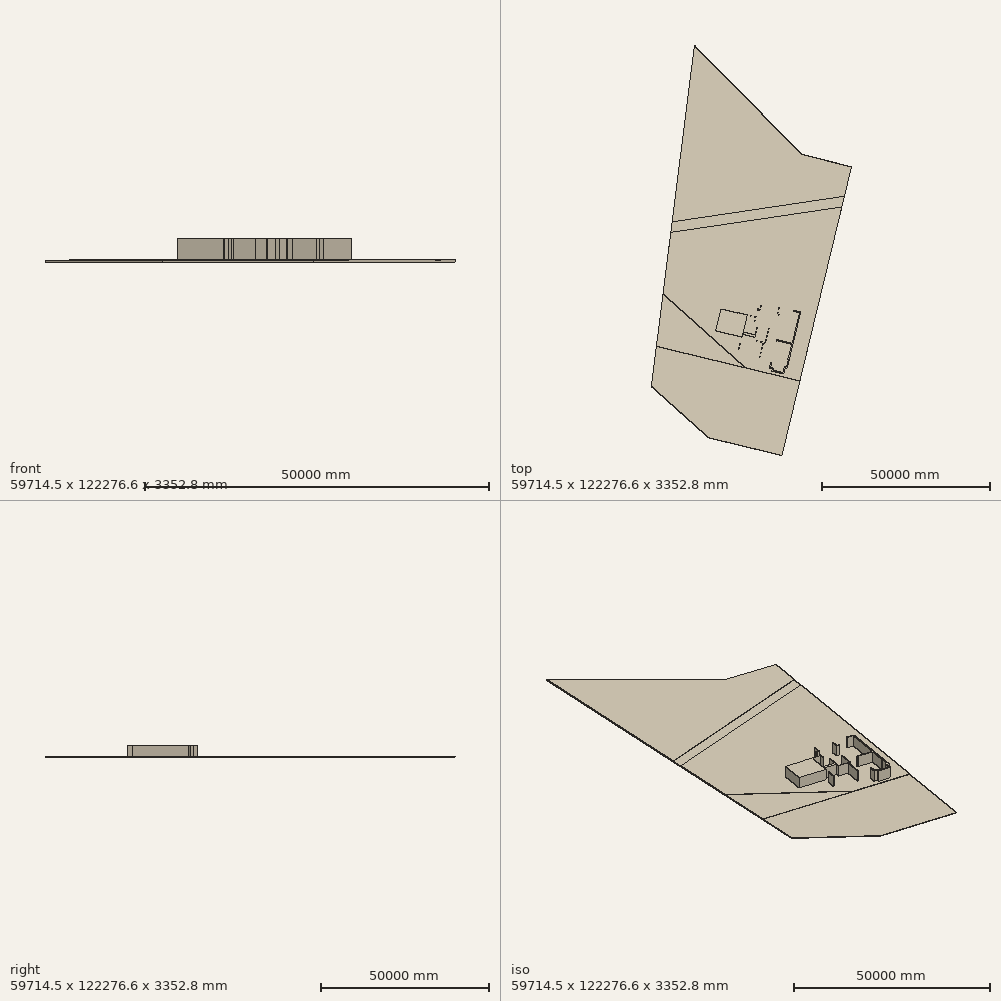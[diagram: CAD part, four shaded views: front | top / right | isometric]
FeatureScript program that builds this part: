
annotation { "Feature Type Name" : "Feature", "Feature Type Description" : "" }
export const myFeature = defineFeature(function(context is Context, id is Id, definition is map)
    precondition{}
    {
        {
            var Q0;
            Q0=qCreatedBy(makeId("Top.planeOp"),FACE);
            var sketch = newSketch(context, id + "F0", { "sketchPlane" : qUnion([Q0])});
            skLineSegment(sketch, "E0", {"start": v(0, 0) * mm, "end": v(31989.83, -32467.96) * mm});
            skLineSegment(sketch, "E1", {"start": v(31989.83, -32467.96) * mm, "end": v(46862.18, -36229.17) * mm});
            skLineSegment(sketch, "E2", {"start": v(46862.18, -36229.17) * mm, "end": v(26112.23, -122276.56) * mm});
            skLineSegment(sketch, "E3", {"start": v(46862.18, -36229.17) * mm, "end": v(46862.18, -51469.17) * mm, "construction": true});
            skLineSegment(sketch, "E4", {"start": v(0, 0) * mm, "end": v(-12852.3, -101676.89) * mm});
            skLineSegment(sketch, "E5", {"start": v(0, 0) * mm, "end": v(0, 15240) * mm, "construction": true});
            skLineSegment(sketch, "E6", {"start": v(26112.23, -122276.56) * mm, "end": v(4230, -116999.76) * mm});
            skLineSegment(sketch, "E7", {"start": v(26112.23, -122276.56) * mm, "end": v(10872.23, -122276.56) * mm, "construction": true});
            skLineSegment(sketch, "E8", {"start": v(4230, -116999.76) * mm, "end": v(-12852.3, -101676.89) * mm});
            skArc(sketch, "E9", {"start": v(-4165.07, -109469.35) * mm, "mid": v(-689.73, -114039.67) * mm, "end": v(4230, -116999.76) * mm, "construction": true});
            skArc(sketch, "E10", {"start": v(-4165.07, -109469.35) * mm, "mid": v(-8132.26, -105153.47) * mm, "end": v(-12852.3, -101676.89) * mm, "construction": true});
            skLineSegment(sketch, "E11", {"start": v(31471.2, -100053.58) * mm, "end": v(-11342.08, -89729.35) * mm});
            skLineSegment(sketch, "E12", {"start": v(-9365.85, -74095.03) * mm, "end": v(15198.72, -96129.54) * mm});
            skLineSegment(sketch, "E13", {"start": v(-6651.63, -52622.31) * mm, "end": v(44754.67, -44968.73) * mm});
            skLineSegment(sketch, "E14", {"start": v(-7048.63, -55763.02) * mm, "end": v(43983.88, -48165.09) * mm});
            skSolve(sketch);
        }
        {
            var Q0;
            {var subQ4=sQuery(id+"F0.wireOp",EDGE,"E0");Q0=makeQuery(id+"F0.imprint","IMPRINT",FACE,{"disambiguationData":[TD([[makeQuery(id+"F0.imprint","IMPRINT",EDGE,{"derivedFrom":subQ4}),-1.0]])]});}
            var Q1;
            {var subQ0=sQuery(id+"F0.wireOp",EDGE,"E13");Q1=makeQuery(id+"F0.imprint","IMPRINT",FACE,{"disambiguationData":[TD([[makeQuery(id+"F0.imprint","IMPRINT",EDGE,{"derivedFrom":subQ0}),-1.0]])]});}
            var Q2;
            {var subQ0=sQuery(id+"F0.wireOp",EDGE,"E12");Q2=makeQuery(id+"F0.imprint","IMPRINT",FACE,{"disambiguationData":[TD([[makeQuery(id+"F0.imprint","IMPRINT",EDGE,{"derivedFrom":subQ0}),1.0]])]});}
            var Q3;
            {var subQ3=sQuery(id+"F0.wireOp",EDGE,"E12");Q3=makeQuery(id+"F0.imprint","IMPRINT",FACE,{"disambiguationData":[TD([[makeQuery(id+"F0.imprint","IMPRINT",EDGE,{"derivedFrom":subQ3}),-1.0]])]});}
            var Q4;
            {var subQ1=sQuery(id+"F0.wireOp",EDGE,"E6");Q4=makeQuery(id+"F0.imprint","IMPRINT",FACE,{"disambiguationData":[TD([[makeQuery(id+"F0.imprint","IMPRINT",EDGE,{"derivedFrom":subQ1}),-1.0]])]});}
            extrude(context, id + "F1", {"entities" : qUnion([Q0, Q1, Q2, Q3, Q4]), "depth" : 304.8 * mm, "offsetDistance" : 25.4 * mm});
        }
        {
            var Q0;
            Q0=makeQuery(id+"F1.opExtrude","CAP_FACE",FACE,{"disambiguationData":[OSD([sQuery(id+"F0.wireOp",EDGE,"E0"),sQuery(id+"F0.wireOp",EDGE,"E1"),sQuery(id+"F0.wireOp",EDGE,"E2"),sQuery(id+"F0.wireOp",EDGE,"E4"),sQuery(id+"F0.wireOp",EDGE,"E6"),sQuery(id+"F0.wireOp",EDGE,"E8")])],"isStart":false});
            var sketch = newSketch(context, id + "F2", { "sketchPlane" : qUnion([Q0])});
            skLineSegment(sketch, "E15.0", {"start": v(-9365.85, -74095.03) * mm, "end": v(15198.72, -96129.54) * mm});
            skLineSegment(sketch, "E16.0", {"start": v(31471.2, -100053.58) * mm, "end": v(-11342.08, -89729.35) * mm});
            skLineSegment(sketch, "E17.0", {"start": v(0, 0) * mm, "end": v(-12852.3, -101676.89) * mm});
            skSolve(sketch);
        }
        {
            var Q0;
            {var subQ0=sQuery(id+"F2.wireOp",EDGE,"E15.0");Q0=makeQuery(id+"F2.imprint","IMPRINT",FACE,{"disambiguationData":[TD([[makeQuery(id+"F2.imprint","IMPRINT",EDGE,{"derivedFrom":subQ0}),-1.0]])]});}
            extrude(context, id + "F3", {"entities" : qUnion([Q0]), "operationType" : NewBodyOperationType.REMOVE, "oppositeDirection" : true, "depth" : 76.2 * mm, "offsetDistance" : 25.4 * mm});
        }
        {
            var Q0;
            Q0=makeQuery(id+"F1.opExtrude","CAP_FACE",FACE,{"disambiguationData":[OSD([sQuery(id+"F0.wireOp",EDGE,"E0"),sQuery(id+"F0.wireOp",EDGE,"E1"),sQuery(id+"F0.wireOp",EDGE,"E2"),sQuery(id+"F0.wireOp",EDGE,"E4"),sQuery(id+"F0.wireOp",EDGE,"E6"),sQuery(id+"F0.wireOp",EDGE,"E8")])],"isStart":false});
            var sketch = newSketch(context, id + "F4", { "sketchPlane" : qUnion([Q0])});
            skLineSegment(sketch, "E18.0", {"start": v(0, 0) * mm, "end": v(-12852.3, -101676.89) * mm});
            skLineSegment(sketch, "E19.0", {"start": v(4230, -116999.76) * mm, "end": v(-12852.3, -101676.89) * mm});
            skLineSegment(sketch, "E20.0", {"start": v(26112.23, -122276.56) * mm, "end": v(4230, -116999.76) * mm});
            skLineSegment(sketch, "E21.0", {"start": v(46862.18, -36229.17) * mm, "end": v(26112.23, -122276.56) * mm});
            skLineSegment(sketch, "E22.0", {"start": v(31471.2, -100053.58) * mm, "end": v(-11342.08, -89729.35) * mm});
            skSolve(sketch);
        }
        {
            var Q0;
            {var subQ4=sQuery(id+"F4.wireOp",EDGE,"E19.0");Q0=makeQuery(id+"F4.imprint","IMPRINT",FACE,{"disambiguationData":[TD([[makeQuery(id+"F4.imprint","IMPRINT",EDGE,{"derivedFrom":subQ4}),-1.0]])]});}
            extrude(context, id + "F5", {"entities" : qUnion([Q0]), "operationType" : NewBodyOperationType.REMOVE, "oppositeDirection" : true, "depth" : 152.4 * mm, "offsetDistance" : 25.4 * mm});
        }
        {
            var Q0;
            Q0=makeQuery(id+"F1.opExtrude","CAP_FACE",FACE,{"disambiguationData":[OSD([sQuery(id+"F0.wireOp",EDGE,"E0"),sQuery(id+"F0.wireOp",EDGE,"E1"),sQuery(id+"F0.wireOp",EDGE,"E2"),sQuery(id+"F0.wireOp",EDGE,"E4"),sQuery(id+"F0.wireOp",EDGE,"E6"),sQuery(id+"F0.wireOp",EDGE,"E8")])],"isStart":false});
            var sketch = newSketch(context, id + "F6", { "sketchPlane" : qUnion([Q0])});
            skLineSegment(sketch, "E23.0", {"start": v(-6651.63, -52622.31) * mm, "end": v(44754.67, -44968.73) * mm});
            skLineSegment(sketch, "E24.0", {"start": v(-7048.63, -55763.02) * mm, "end": v(43983.88, -48165.09) * mm});
            skLineSegment(sketch, "E25.0", {"start": v(0, 0) * mm, "end": v(-12852.3, -101676.89) * mm});
            skLineSegment(sketch, "E26.0", {"start": v(46862.18, -36229.17) * mm, "end": v(26112.23, -122276.56) * mm});
            skSolve(sketch);
        }
        {
            var Q0;
            {var subQ0=sQuery(id+"F6.wireOp",EDGE,"E23.0");Q0=makeQuery(id+"F6.imprint","IMPRINT",FACE,{"disambiguationData":[TD([[makeQuery(id+"F6.imprint","IMPRINT",EDGE,{"derivedFrom":subQ0}),-1.0]])]});}
            extrude(context, id + "F7", {"entities" : qUnion([Q0]), "operationType" : NewBodyOperationType.REMOVE, "oppositeDirection" : true, "depth" : 152.4 * mm, "offsetDistance" : 25.4 * mm});
        }
        {
            var Q0;
            {var subQ0=sQuery(id+"F0.wireOp",EDGE,"E4");var subQ1=sQuery(id+"F0.wireOp",EDGE,"E2");Q0=makeQuery(id+"F7.boolean.opBoolean","SPLIT",FACE,{"disambiguationData":[TD([makeQuery(id+"F3.boolean.opBoolean","COPY",FACE,{"derivedFrom":makeQuery(id+"F3.opExtrude","SWEPT_FACE",FACE,{"disambiguationData":[OSD([sQuery(id+"F2.wireOp",EDGE,"E15.0")])]})})])],"derivedFrom":makeQuery(id+"F1.opExtrude","CAP_FACE",FACE,{"disambiguationData":[OSD([sQuery(id+"F0.wireOp",EDGE,"E0"),sQuery(id+"F0.wireOp",EDGE,"E1"),subQ1,subQ0,sQuery(id+"F0.wireOp",EDGE,"E6"),sQuery(id+"F0.wireOp",EDGE,"E8")])],"isStart":false})});}
            var sketch = newSketch(context, id + "F8", { "sketchPlane" : qUnion([Q0])});
            skLineSegment(sketch, "E27", {"start": v(27669.68, -96315.03) * mm, "end": v(31724.64, -79499.64) * mm});
            skPoint(sketch, "E28.orphan", {"position": v(31471.2, -100053.58) * mm});
            skLineSegment(sketch, "E29", {"start": v(-5717.12, -79311.3) * mm, "end": v(3764.68, -81597.8) * mm});
            skLineSegment(sketch, "E30", {"start": v(3764.68, -81597.8) * mm, "end": v(7766.05, -65004.64) * mm});
            skLineSegment(sketch, "E31", {"start": v(7766.05, -65004.64) * mm, "end": v(-1715.76, -62718.14) * mm});
            skLineSegment(sketch, "E32", {"start": v(-1715.76, -62718.14) * mm, "end": v(-5717.12, -79311.3) * mm});
            skLineSegment(sketch, "E33", {"start": v(-5145.5, -76940.85) * mm, "end": v(-2182.44, -77655.38) * mm});
            skLineSegment(sketch, "E34", {"start": v(-2182.44, -77655.38) * mm, "end": v(-2754.06, -80025.83) * mm});
            skLineSegment(sketch, "E35", {"start": v(-5145.5, -76940.85) * mm, "end": v(-9590.1, -75869.05) * mm});
            skLineSegment(sketch, "E36", {"start": v(-2182.44, -77655.38) * mm, "end": v(1247.3, -63432.67) * mm});
            skLineSegment(sketch, "E37", {"start": v(4934.3, -91780.7) * mm, "end": v(-10343.91, -88096.42) * mm});
            skLineSegment(sketch, "E38.0", {"start": v(4230, -116999.76) * mm, "end": v(-12852.3, -101676.89) * mm});
            skLineSegment(sketch, "E39", {"start": v(-2047.33, -90097.1) * mm, "end": v(-6264.7, -107585.98) * mm});
            skLineSegment(sketch, "E40", {"start": v(-5603, -89239.67) * mm, "end": v(-9358.03, -104811.25) * mm});
            skArc(sketch, "E41", {"start": v(-6746.26, -93980.57) * mm, "mid": v(-7326.44, -90293.4) * mm, "end": v(-10343.91, -88096.42) * mm});
            skLineSegment(sketch, "E42", {"start": v(-8087.58, -78739.68) * mm, "end": v(-10343.91, -88096.42) * mm});
            skLineSegment(sketch, "E43", {"start": v(-5717.12, -79311.3) * mm, "end": v(-8087.58, -78739.68) * mm});
            skLineSegment(sketch, "E44", {"start": v(22775.38, -94507.71) * mm, "end": v(22346.66, -96285.55) * mm});
            skLineSegment(sketch, "E45", {"start": v(22346.66, -96285.55) * mm, "end": v(23235.58, -96499.91) * mm});
            skLineSegment(sketch, "E46", {"start": v(23235.58, -96499.91) * mm, "end": v(23092.67, -97092.52) * mm});
            skLineSegment(sketch, "E47", {"start": v(23092.67, -97092.52) * mm, "end": v(26648.35, -97949.96) * mm});
            skLineSegment(sketch, "E48", {"start": v(26648.35, -97949.96) * mm, "end": v(27077.07, -96172.12) * mm});
            skLineSegment(sketch, "E49", {"start": v(12775.04, -92096.18) * mm, "end": v(13945.08, -87244.16) * mm});
            skLineSegment(sketch, "E50", {"start": v(13945.08, -87244.16) * mm, "end": v(5981.84, -85323.86) * mm});
            skLineSegment(sketch, "E51", {"start": v(5981.84, -85323.86) * mm, "end": v(7696.71, -78212.5) * mm});
            skLineSegment(sketch, "E52", {"start": v(14020.33, -75230.32) * mm, "end": v(31724.64, -79499.64) * mm});
            skLineSegment(sketch, "E53.trimOffspring", {"start": v(27077.07, -96172.12) * mm, "end": v(27669.68, -96315.03) * mm});
            skLineSegment(sketch, "E54.0", {"start": v(6349.6, -85099) * mm, "end": v(7921.57, -78580.26) * mm});
            skLineSegment(sketch, "E54.1", {"start": v(23460.43, -96867.67) * mm, "end": v(26423.5, -97582.2) * mm});
            skLineSegment(sketch, "E54.2", {"start": v(26423.5, -97582.2) * mm, "end": v(26852.22, -95804.36) * mm});
            skLineSegment(sketch, "E54.3", {"start": v(26852.22, -95804.36) * mm, "end": v(27444.83, -95947.27) * mm});
            skLineSegment(sketch, "E54.4", {"start": v(27444.83, -95947.27) * mm, "end": v(28016.45, -93576.82) * mm});
            skLineSegment(sketch, "E54.5", {"start": v(23603.34, -96275.06) * mm, "end": v(23460.43, -96867.67) * mm});
            skLineSegment(sketch, "E54.6", {"start": v(14245.18, -75598.08) * mm, "end": v(19282.4, -76812.78) * mm});
            skLineSegment(sketch, "E54.7", {"start": v(22714.42, -96060.7) * mm, "end": v(23603.34, -96275.06) * mm});
            skLineSegment(sketch, "E54.8", {"start": v(23143.14, -94282.86) * mm, "end": v(22714.42, -96060.7) * mm});
            skLineSegment(sketch, "E54.9", {"start": v(13142.8, -91871.32) * mm, "end": v(23143.14, -94282.86) * mm});
            skLineSegment(sketch, "E54.10", {"start": v(13142.8, -91871.32) * mm, "end": v(14312.84, -87019.3) * mm});
            skLineSegment(sketch, "E54.11", {"start": v(14312.84, -87019.3) * mm, "end": v(6349.6, -85099) * mm});
            skLineSegment(sketch, "E55", {"start": v(20619.6, -88657.73) * mm, "end": v(19476.35, -93398.63) * mm});
            skLineSegment(sketch, "E56.0", {"start": v(20508.48, -88630.93) * mm, "end": v(19365.23, -93371.83) * mm});
            skLineSegment(sketch, "E57", {"start": v(17505, -84183.4) * mm, "end": v(18255.26, -81072.19) * mm});
            skLineSegment(sketch, "E58", {"start": v(17821.54, -83358.32) * mm, "end": v(19393.5, -76839.58) * mm});
            skLineSegment(sketch, "E59", {"start": v(7921.57, -78580.26) * mm, "end": v(18255.26, -81072.19) * mm});
            skLineSegment(sketch, "E60", {"start": v(14020.33, -75230.32) * mm, "end": v(12993.2, -79489.73) * mm});
            skLineSegment(sketch, "E61", {"start": v(12993.2, -79489.73) * mm, "end": v(7696.71, -78212.5) * mm});
            skLineSegment(sketch, "E62", {"start": v(14245.18, -75598.08) * mm, "end": v(13218.05, -79857.49) * mm});
            skLineSegment(sketch, "E63", {"start": v(13244.84, -79746.37) * mm, "end": v(18282.05, -80961.07) * mm});
            skLineSegment(sketch, "E64", {"start": v(23143.14, -94282.86) * mm, "end": v(23571.86, -92505.02) * mm});
            skLineSegment(sketch, "E65", {"start": v(23032.02, -94256.07) * mm, "end": v(24603.99, -87737.32) * mm});
            skLineSegment(sketch, "E66", {"start": v(24175.27, -89515.16) * mm, "end": v(20619.6, -88657.73) * mm});
            skLineSegment(sketch, "E67", {"start": v(19833.61, -91917.1) * mm, "end": v(21018.84, -92202.9) * mm});
            skLineSegment(sketch, "E68", {"start": v(21018.84, -92202.9) * mm, "end": v(21519, -90128.76) * mm});
            skLineSegment(sketch, "E69", {"start": v(21519, -90128.76) * mm, "end": v(23889.46, -90700.39) * mm});
            skLineSegment(sketch, "E70", {"start": v(23571.86, -92505.02) * mm, "end": v(28016.45, -93576.82) * mm});
            skLineSegment(sketch, "E71", {"start": v(23828.5, -92253.37) * mm, "end": v(27982.96, -93255.2) * mm});
            skLineSegment(sketch, "E72.trimOffspring", {"start": v(18282.05, -80961.07) * mm, "end": v(19282.4, -76812.78) * mm});
            skLineSegment(sketch, "E73", {"start": v(28983.3, -89106.91) * mm, "end": v(24828.84, -88105.08) * mm});
            skLineSegment(sketch, "E74", {"start": v(27982.96, -93255.2) * mm, "end": v(28983.3, -89106.91) * mm});
            skLineSegment(sketch, "E75", {"start": v(23828.5, -92253.37) * mm, "end": v(24828.84, -88105.08) * mm});
            skLineSegment(sketch, "E76.trimOffspring", {"start": v(29159.7, -88835.91) * mm, "end": v(31356.88, -79724.5) * mm});
            skLineSegment(sketch, "E77", {"start": v(29159.7, -88835.91) * mm, "end": v(24603.99, -87737.32) * mm});
            skLineSegment(sketch, "E78", {"start": v(26023.36, -78438.34) * mm, "end": v(24951.57, -82882.93) * mm});
            skLineSegment(sketch, "E79", {"start": v(24951.57, -82882.93) * mm, "end": v(30285.09, -84169.09) * mm});
            skLineSegment(sketch, "E80", {"start": v(25912.25, -78411.54) * mm, "end": v(24340.28, -84930.28) * mm});
            skLineSegment(sketch, "E81", {"start": v(24924.77, -82994.05) * mm, "end": v(30258.3, -84280.2) * mm});
            skLineSegment(sketch, "E82", {"start": v(21057.5, -78390.48) * mm, "end": v(23724.26, -79033.55) * mm});
            skLineSegment(sketch, "E83", {"start": v(23724.26, -79033.55) * mm, "end": v(23474.18, -80070.63) * mm});
            skLineSegment(sketch, "E84", {"start": v(23474.18, -80070.63) * mm, "end": v(20807.42, -79427.55) * mm});
            skLineSegment(sketch, "E85", {"start": v(20807.42, -79427.55) * mm, "end": v(21057.5, -78390.48) * mm});
            skLineSegment(sketch, "E86", {"start": v(12993.2, -79489.73) * mm, "end": v(12921.74, -79786.03) * mm});
            skLineSegment(sketch, "E87", {"start": v(17821.54, -83358.32) * mm, "end": v(24340.28, -84930.28) * mm});
            skLineSegment(sketch, "E88", {"start": v(25961.85, -83244.13) * mm, "end": v(25553.97, -84935.55) * mm});
            skLineSegment(sketch, "E89", {"start": v(17794.75, -83469.43) * mm, "end": v(24424.6, -85068.2) * mm});
            skLineSegment(sketch, "E90", {"start": v(24424.6, -85068.2) * mm, "end": v(24924.77, -82994.05) * mm});
            skLineSegment(sketch, "E91", {"start": v(25054.81, -81967.22) * mm, "end": v(24462.2, -81824.31) * mm});
            skLineSegment(sketch, "E92", {"start": v(24462.2, -81824.31) * mm, "end": v(23890.58, -84194.76) * mm});
            skLineSegment(sketch, "E93", {"start": v(23890.58, -84194.76) * mm, "end": v(18927.44, -82997.93) * mm});
            skLineSegment(sketch, "E94", {"start": v(18807.15, -81871.54) * mm, "end": v(19128.68, -80538.16) * mm});
            skLineSegment(sketch, "E95", {"start": v(19128.68, -80538.16) * mm, "end": v(18536.07, -80395.25) * mm});
            skLineSegment(sketch, "E96", {"start": v(20165.76, -80788.24) * mm, "end": v(19879.94, -81973.47) * mm});
            skLineSegment(sketch, "E97", {"start": v(19879.94, -81973.47) * mm, "end": v(23139.32, -82759.45) * mm});
            skLineSegment(sketch, "E98", {"start": v(23139.32, -82759.45) * mm, "end": v(23425.13, -81574.23) * mm});
            skLineSegment(sketch, "E99", {"start": v(23425.13, -81574.23) * mm, "end": v(20165.76, -80788.24) * mm});
            skLineSegment(sketch, "E100", {"start": v(18920.13, -78802.6) * mm, "end": v(19512.74, -78945.51) * mm});
            skLineSegment(sketch, "E101", {"start": v(19512.74, -78945.51) * mm, "end": v(19986.12, -76982.48) * mm});
            skLineSegment(sketch, "E102.0", {"start": v(19597.06, -79083.42) * mm, "end": v(20097.24, -77009.28) * mm});
            skLineSegment(sketch, "E102.1", {"start": v(18893.34, -78913.72) * mm, "end": v(19597.06, -79083.42) * mm});
            skLineSegment(sketch, "E103", {"start": v(19393.5, -76839.58) * mm, "end": v(25912.25, -78411.54) * mm});
            skLineSegment(sketch, "E104.trimOffspring", {"start": v(26023.36, -78438.34) * mm, "end": v(31356.88, -79724.5) * mm});
            skLineSegment(sketch, "E105", {"start": v(27837.43, -93533.65) * mm, "end": v(27908.89, -93237.34) * mm});
            skLineSegment(sketch, "E106", {"start": v(26948.51, -93319.29) * mm, "end": v(27019.97, -93022.98) * mm});
            skLineSegment(sketch, "E107", {"start": v(26972.33, -93220.52) * mm, "end": v(27861.25, -93434.88) * mm});
            skLineSegment(sketch, "E108", {"start": v(26963.4, -93257.56) * mm, "end": v(27852.32, -93471.92) * mm});
            skLineSegment(sketch, "E109", {"start": v(24810.98, -88179.16) * mm, "end": v(24514.67, -88107.7) * mm});
            skLineSegment(sketch, "E110", {"start": v(24300.31, -88996.63) * mm, "end": v(24596.62, -89068.08) * mm});
            skLineSegment(sketch, "E111", {"start": v(24362.04, -89011.51) * mm, "end": v(24576.4, -88122.6) * mm});
            skLineSegment(sketch, "E112", {"start": v(24399.08, -89020.44) * mm, "end": v(24613.44, -88131.52) * mm});
            skLineSegment(sketch, "E113", {"start": v(15884.8, -80500.56) * mm, "end": v(14312.84, -87019.3) * mm});
            skLineSegment(sketch, "E114", {"start": v(18807.15, -81871.54) * mm, "end": v(18214.53, -81728.63) * mm});
            skLineSegment(sketch, "E115", {"start": v(12775.04, -92096.18) * mm, "end": v(23071.68, -94579.17) * mm});
            skLineSegment(sketch, "E116", {"start": v(15741.9, -81093.17) * mm, "end": v(18112.35, -81664.8) * mm});
            skLineSegment(sketch, "E117", {"start": v(17772.95, -83072.25) * mm, "end": v(17884.06, -83099.05) * mm});
            skLineSegment(sketch, "E118", {"start": v(17987.3, -82183.34) * mm, "end": v(18098.42, -82210.13) * mm});
            skLineSegment(sketch, "E119", {"start": v(15291.38, -82473.84) * mm, "end": v(15402.5, -82500.63) * mm});
            skLineSegment(sketch, "E120", {"start": v(15505.74, -81584.92) * mm, "end": v(15616.86, -81611.71) * mm});
            skLineSegment(sketch, "E121", {"start": v(15561.3, -81598.31) * mm, "end": v(15346.94, -82487.23) * mm});
            skLineSegment(sketch, "E122", {"start": v(25412.08, -80485.69) * mm, "end": v(24708.35, -80315.99) * mm});
            skLineSegment(sketch, "E123", {"start": v(24708.35, -80315.99) * mm, "end": v(25208.52, -78241.84) * mm});
            skLineSegment(sketch, "E124", {"start": v(18460.68, -80220.3) * mm, "end": v(18571.8, -80247.1) * mm});
            skLineSegment(sketch, "E125", {"start": v(18746.5, -79035.08) * mm, "end": v(18857.6, -79061.87) * mm});
            skLineSegment(sketch, "E126", {"start": v(19210.94, -77109.09) * mm, "end": v(19322.05, -77135.88) * mm});
            skLineSegment(sketch, "E127", {"start": v(18877.5, -78491.85) * mm, "end": v(18988.6, -78518.65) * mm});
            skLineSegment(sketch, "E128", {"start": v(19044.22, -77800.47) * mm, "end": v(19155.33, -77827.26) * mm});
            skLineSegment(sketch, "E129", {"start": v(18933.05, -78505.25) * mm, "end": v(19099.77, -77813.87) * mm});
            skLineSegment(sketch, "E130", {"start": v(19099.77, -77813.87) * mm, "end": v(19266.5, -77122.48) * mm});
            skLineSegment(sketch, "E131", {"start": v(25319.64, -78268.64) * mm, "end": v(24846.26, -80231.67) * mm});
            skLineSegment(sketch, "E132", {"start": v(24846.26, -80231.67) * mm, "end": v(25438.87, -80374.57) * mm});
            skLineSegment(sketch, "E133", {"start": v(26072.96, -83270.93) * mm, "end": v(25665.08, -84962.34) * mm});
            skLineSegment(sketch, "E134", {"start": v(25715.7, -84752.46) * mm, "end": v(29901.03, -85761.73) * mm});
            skLineSegment(sketch, "E135", {"start": v(25688.9, -84863.58) * mm, "end": v(29874.23, -85872.85) * mm});
            skLineSegment(sketch, "E136", {"start": v(28554.53, -83869.35) * mm, "end": v(28197.26, -85350.88) * mm});
            skLineSegment(sketch, "E137", {"start": v(28443.41, -83842.55) * mm, "end": v(28086.15, -85324.08) * mm});
            skLineSegment(sketch, "E138", {"start": v(27702.65, -83663.92) * mm, "end": v(27345.38, -85145.45) * mm});
            skLineSegment(sketch, "E139", {"start": v(25941.96, -83814.16) * mm, "end": v(26830.88, -84028.52) * mm});
            skLineSegment(sketch, "E140", {"start": v(26830.88, -84028.52) * mm, "end": v(26961.88, -83485.29) * mm});
            skLineSegment(sketch, "E141", {"start": v(27085.34, -83515.06) * mm, "end": v(27013.89, -83811.37) * mm});
            skLineSegment(sketch, "E142", {"start": v(27013.89, -83811.37) * mm, "end": v(27507.73, -83930.45) * mm});
            skLineSegment(sketch, "E143", {"start": v(27507.73, -83930.45) * mm, "end": v(27579.19, -83634.15) * mm});
            skLineSegment(sketch, "E144", {"start": v(27112.66, -83835.18) * mm, "end": v(26999.52, -84304.34) * mm});
            skLineSegment(sketch, "E145", {"start": v(26999.52, -84304.34) * mm, "end": v(27295.83, -84375.79) * mm});
            skLineSegment(sketch, "E146", {"start": v(27295.83, -84375.79) * mm, "end": v(27408.96, -83906.64) * mm});
            skLineSegment(sketch, "E147", {"start": v(25762.98, -84881.44) * mm, "end": v(25789.77, -84770.32) * mm});
            skLineSegment(sketch, "E148", {"start": v(26355.6, -85024.34) * mm, "end": v(26382.39, -84913.23) * mm});
            skLineSegment(sketch, "E149", {"start": v(25776.38, -84825.88) * mm, "end": v(26368.99, -84968.79) * mm});
            skArc(sketch, "E150", {"start": v(26368.99, -84968.79) * mm, "mid": v(26275.53, -84475.95) * mm, "end": v(25844.08, -84220.05) * mm, "construction": true});
            skLineSegment(sketch, "E151", {"start": v(28340.17, -84758.27) * mm, "end": v(30043.93, -85169.12) * mm});
            skLineSegment(sketch, "E152", {"start": v(28366.96, -84647.15) * mm, "end": v(30070.73, -85058) * mm});
            skLineSegment(sketch, "E153", {"start": v(29278.79, -88342.07) * mm, "end": v(27303.41, -87865.72) * mm});
            skLineSegment(sketch, "E154", {"start": v(27303.41, -87865.72) * mm, "end": v(27755.95, -85989.1) * mm});
            skLineSegment(sketch, "E155", {"start": v(27755.95, -85989.1) * mm, "end": v(29731.32, -86465.46) * mm});
            skLineSegment(sketch, "E156", {"start": v(28296.03, -85374.7) * mm, "end": v(28269.24, -85485.81) * mm});
            skLineSegment(sketch, "E157", {"start": v(29777.56, -85731.96) * mm, "end": v(29750.77, -85843.08) * mm});
            skLineSegment(sketch, "E158", {"start": v(29036.8, -85553.33) * mm, "end": v(29010, -85664.44) * mm});
            skLineSegment(sketch, "E159", {"start": v(28282.63, -85430.25) * mm, "end": v(29023.4, -85608.89) * mm});
            skLineSegment(sketch, "E160", {"start": v(29023.4, -85608.89) * mm, "end": v(29764.17, -85787.52) * mm});
            skLineSegment(sketch, "E161", {"start": v(26429.67, -85042.2) * mm, "end": v(26197.45, -86005.2) * mm});
            skLineSegment(sketch, "E162", {"start": v(26197.45, -86005.2) * mm, "end": v(25456.68, -85826.57) * mm});
            skLineSegment(sketch, "E163", {"start": v(26540.78, -85069) * mm, "end": v(26281.77, -86143.11) * mm});
            skLineSegment(sketch, "E164", {"start": v(26281.77, -86143.11) * mm, "end": v(25429.88, -85937.69) * mm});
            skLineSegment(sketch, "E165", {"start": v(26405.85, -85140.98) * mm, "end": v(26516.97, -85167.77) * mm});
            skLineSegment(sketch, "E166", {"start": v(26215.3, -85931.13) * mm, "end": v(26326.42, -85957.92) * mm});
            skLineSegment(sketch, "E167", {"start": v(26461.4, -85154.37) * mm, "end": v(26270.87, -85944.52) * mm});
            skArc(sketch, "E168", {"start": v(26270.87, -85944.52) * mm, "mid": v(26927.99, -85819.92) * mm, "end": v(27269.18, -85244.65) * mm, "construction": true});
            skLineSegment(sketch, "E169", {"start": v(25363.43, -85725.7) * mm, "end": v(25474.54, -85752.5) * mm});
            skLineSegment(sketch, "E170", {"start": v(25553.97, -84935.55) * mm, "end": v(25665.08, -84962.34) * mm});
            skLineSegment(sketch, "E171.trimOffspring", {"start": v(25363.43, -85725.7) * mm, "end": v(24863.26, -87799.85) * mm});
            skLineSegment(sketch, "E172.trimOffspring", {"start": v(25474.54, -85752.5) * mm, "end": v(24974.37, -87826.64) * mm});
            skLineSegment(sketch, "E173", {"start": v(14201.72, -86992.5) * mm, "end": v(15773.69, -80473.77) * mm});
            skLineSegment(sketch, "E174", {"start": v(23000.54, -90486.03) * mm, "end": v(23286.35, -89300.8) * mm});
            skLineSegment(sketch, "E175", {"start": v(20809.72, -93720.17) * mm, "end": v(20738.27, -94016.47) * mm});
            skLineSegment(sketch, "E176", {"start": v(21698.64, -93934.53) * mm, "end": v(21627.2, -94230.83) * mm});
            skLineSegment(sketch, "E177", {"start": v(20774, -93868.32) * mm, "end": v(21662.92, -94082.68) * mm});
            skArc(sketch, "E178", {"start": v(24399.08, -89020.44) * mm, "mid": v(25122.55, -88891.09) * mm, "end": v(25517.13, -88271.06) * mm, "construction": true});
            skArc(sketch, "E179", {"start": v(26972.33, -93220.52) * mm, "mid": v(27417.21, -92635.53) * mm, "end": v(28148.94, -92566.91) * mm, "construction": true});
            skLineSegment(sketch, "E180", {"start": v(28435.5, -91378.6) * mm, "end": v(27052.74, -91045.15) * mm});
            skLineSegment(sketch, "E181", {"start": v(26412.84, -90773.26) * mm, "end": v(25933.51, -92760.99) * mm});
            skLineSegment(sketch, "E182", {"start": v(25822.4, -92734.2) * mm, "end": v(26301.73, -90746.47) * mm});
            skLineSegment(sketch, "E183", {"start": v(27079.53, -90934.03) * mm, "end": v(28462.3, -91267.48) * mm});
            skLineSegment(sketch, "E184", {"start": v(27872.16, -88838.96) * mm, "end": v(27401.76, -90789.65) * mm});
            skLineSegment(sketch, "E185", {"start": v(27401.76, -90789.65) * mm, "end": v(28512.9, -91057.6) * mm});
            skLineSegment(sketch, "E186", {"start": v(27694.73, -91199.96) * mm, "end": v(27444.65, -92237.04) * mm});
            skLineSegment(sketch, "E187", {"start": v(27444.65, -92237.04) * mm, "end": v(27987.88, -92368.03) * mm});
            skLineSegment(sketch, "E188", {"start": v(27987.88, -92368.03) * mm, "end": v(28237.96, -91330.96) * mm});
            skLineSegment(sketch, "E189", {"start": v(27798.08, -88821.1) * mm, "end": v(27530.13, -89932.25) * mm});
            skLineSegment(sketch, "E190", {"start": v(27530.13, -89932.25) * mm, "end": v(25579.45, -89461.85) * mm});
            skLineSegment(sketch, "E191", {"start": v(25579.45, -89461.85) * mm, "end": v(25847.4, -88350.7) * mm});
            skLineSegment(sketch, "E192", {"start": v(27497.2, -91152.33) * mm, "end": v(27306.65, -91942.48) * mm});
            skLineSegment(sketch, "E193", {"start": v(27306.65, -91942.48) * mm, "end": v(26936.27, -91853.16) * mm});
            skLineSegment(sketch, "E194", {"start": v(26936.27, -91853.16) * mm, "end": v(27126.81, -91063.01) * mm});
            skLineSegment(sketch, "E195", {"start": v(24281.04, -90376.77) * mm, "end": v(26256.41, -90853.12) * mm});
            skLineSegment(sketch, "E196", {"start": v(26256.41, -90853.12) * mm, "end": v(25803.88, -92729.73) * mm});
            skLineSegment(sketch, "E197", {"start": v(27079.53, -90934.03) * mm, "end": v(27052.74, -91045.15) * mm});
            skLineSegment(sketch, "E198", {"start": v(26301.73, -90746.47) * mm, "end": v(26412.84, -90773.26) * mm});
            skLineSegment(sketch, "E199", {"start": v(13072.76, -90861.57) * mm, "end": v(13369.06, -90933.02) * mm});
            skLineSegment(sketch, "E200", {"start": v(13715.83, -88194.8) * mm, "end": v(14012.14, -88266.26) * mm});
            skLineSegment(sketch, "E201", {"start": v(13863.99, -88230.53) * mm, "end": v(13220.9, -90897.3) * mm});
            skLineSegment(sketch, "E202", {"start": v(30171.65, -79438.68) * mm, "end": v(31071.07, -80909.72) * mm});
            skLineSegment(sketch, "E203", {"start": v(30928.16, -81502.33) * mm, "end": v(30236.78, -81335.6) * mm});
            skLineSegment(sketch, "E204", {"start": v(30236.78, -81335.6) * mm, "end": v(29879.52, -82817.14) * mm});
            skLineSegment(sketch, "E205", {"start": v(29879.52, -82817.14) * mm, "end": v(30570.9, -82983.86) * mm});
            skLineSegment(sketch, "E206", {"start": v(25090.54, -81819.07) * mm, "end": v(25201.65, -81845.86) * mm});
            skLineSegment(sketch, "E207", {"start": v(25376.35, -80633.84) * mm, "end": v(25487.47, -80660.63) * mm});
            skLineSegment(sketch, "E208", {"start": v(24998.85, -83011.91) * mm, "end": v(25025.65, -82900.8) * mm});
            skLineSegment(sketch, "E209", {"start": v(25887.77, -83226.27) * mm, "end": v(25914.57, -83115.16) * mm});
            skLineSegment(sketch, "E210", {"start": v(25012.25, -82956.35) * mm, "end": v(25901.17, -83170.71) * mm});
            skArc(sketch, "E211", {"start": v(25901.17, -83170.71) * mm, "mid": v(25771.81, -82447.25) * mm, "end": v(25151.79, -82052.66) * mm, "construction": true});
            skLineSegment(sketch, "E212", {"start": v(28653.3, -83893.16) * mm, "end": v(28680.1, -83782.05) * mm});
            skLineSegment(sketch, "E213", {"start": v(29420.86, -83960.68) * mm, "end": v(29394.06, -84071.8) * mm});
            skLineSegment(sketch, "E214", {"start": v(30161.62, -84139.31) * mm, "end": v(30134.83, -84250.43) * mm});
            skLineSegment(sketch, "E215", {"start": v(28666.7, -83837.6) * mm, "end": v(29407.46, -84016.24) * mm});
            skLineSegment(sketch, "E216", {"start": v(29407.46, -84016.24) * mm, "end": v(30148.23, -84194.87) * mm});
            skLineSegment(sketch, "E217", {"start": v(26761.5, -78302.8) * mm, "end": v(26690.05, -78599.1) * mm});
            skLineSegment(sketch, "E218", {"start": v(27502.27, -78481.43) * mm, "end": v(27430.82, -78777.74) * mm});
            skLineSegment(sketch, "E219", {"start": v(27798.58, -78552.88) * mm, "end": v(27727.13, -78849.2) * mm});
            skLineSegment(sketch, "E220", {"start": v(28539.35, -78731.52) * mm, "end": v(28467.9, -79027.82) * mm});
            skLineSegment(sketch, "E221", {"start": v(28835.65, -78802.97) * mm, "end": v(28764.2, -79099.28) * mm});
            skLineSegment(sketch, "E222", {"start": v(29576.42, -78981.6) * mm, "end": v(29504.96, -79277.9) * mm});
            skLineSegment(sketch, "E223", {"start": v(27466.55, -78629.58) * mm, "end": v(26725.78, -78450.95) * mm});
            skLineSegment(sketch, "E224", {"start": v(27762.85, -78701.04) * mm, "end": v(28503.62, -78879.67) * mm});
            skLineSegment(sketch, "E225", {"start": v(28799.93, -78951.12) * mm, "end": v(29540.7, -79129.76) * mm});
            skLineSegment(sketch, "E226", {"start": v(26511.22, -82266.17) * mm, "end": v(26296.86, -83155.09) * mm});
            skLineSegment(sketch, "E227", {"start": v(26296.86, -83155.09) * mm, "end": v(28222.85, -83619.53) * mm});
            skLineSegment(sketch, "E228", {"start": v(28222.85, -83619.53) * mm, "end": v(28437.2, -82730.61) * mm});
            skLineSegment(sketch, "E229", {"start": v(28437.2, -82730.61) * mm, "end": v(26511.22, -82266.17) * mm});
            skLineSegment(sketch, "E230", {"start": v(27492.99, -78844.99) * mm, "end": v(29418.98, -79309.43) * mm});
            skLineSegment(sketch, "E231", {"start": v(29418.98, -79309.43) * mm, "end": v(29204.62, -80198.35) * mm});
            skLineSegment(sketch, "E232", {"start": v(29204.62, -80198.35) * mm, "end": v(27278.63, -79733.9) * mm});
            skLineSegment(sketch, "E233", {"start": v(27278.63, -79733.9) * mm, "end": v(27492.99, -78844.99) * mm});
            skLineSegment(sketch, "E234", {"start": v(25456.74, -80300.5) * mm, "end": v(25567.85, -80327.29) * mm});
            skLineSegment(sketch, "E235", {"start": v(25671.1, -79411.58) * mm, "end": v(25782.21, -79438.37) * mm});
            skLineSegment(sketch, "E236", {"start": v(25885.45, -78522.66) * mm, "end": v(25996.57, -78549.45) * mm});
            skLineSegment(sketch, "E237", {"start": v(25941.01, -78536.05) * mm, "end": v(25726.65, -79424.97) * mm});
            skLineSegment(sketch, "E238", {"start": v(25726.65, -79424.97) * mm, "end": v(25512.3, -80313.9) * mm});
            skLineSegment(sketch, "E239", {"start": v(15134.55, -83611.78) * mm, "end": v(17505, -84183.4) * mm});
            skLineSegment(sketch, "E240", {"start": v(15107.75, -83722.9) * mm, "end": v(17589.32, -84321.31) * mm});
            skLineSegment(sketch, "E241", {"start": v(17589.32, -84321.31) * mm, "end": v(17794.75, -83469.43) * mm});
            skLineSegment(sketch, "E242", {"start": v(15277.45, -83019.17) * mm, "end": v(17647.9, -83590.8) * mm});
            skLineSegment(sketch, "E243", {"start": v(15366.77, -82648.78) * mm, "end": v(17737.22, -83220.4) * mm});
            skLineSegment(sketch, "E244", {"start": v(15652.58, -81463.56) * mm, "end": v(18023.03, -82035.18) * mm});
            skLineSegment(sketch, "E245", {"start": v(14964.85, -84315.5) * mm, "end": v(17446.41, -84913.93) * mm});
            skLineSegment(sketch, "E246", {"start": v(17446.41, -84913.93) * mm, "end": v(17589.32, -84321.31) * mm});
            skLineSegment(sketch, "E247", {"start": v(14679.03, -85500.73) * mm, "end": v(18123.6, -86331.37) * mm});
            skLineSegment(sketch, "E248", {"start": v(22239.34, -84541.23) * mm, "end": v(21212.2, -88800.63) * mm});
            skLineSegment(sketch, "E249", {"start": v(22128.23, -84514.43) * mm, "end": v(21127.89, -88662.72) * mm});
            skLineSegment(sketch, "E250", {"start": v(18725.95, -84321.06) * mm, "end": v(21392.7, -84964.14) * mm});
            skLineSegment(sketch, "E251", {"start": v(21392.7, -84964.14) * mm, "end": v(20678.18, -87927.2) * mm});
            skLineSegment(sketch, "E252", {"start": v(14509.33, -86204.46) * mm, "end": v(17953.9, -87035.1) * mm});
            skLineSegment(sketch, "E253", {"start": v(18757.74, -83701.65) * mm, "end": v(17980.7, -86923.99) * mm});
            skLineSegment(sketch, "E254", {"start": v(18868.86, -83728.45) * mm, "end": v(17868.52, -87876.74) * mm});
            skLineSegment(sketch, "E255.trimOffspring", {"start": v(18604.03, -87427.03) * mm, "end": v(20678.18, -87927.2) * mm});
            skLineSegment(sketch, "E256", {"start": v(14536.13, -86093.35) * mm, "end": v(17977.27, -86923.16) * mm});
            skLineSegment(sketch, "E257", {"start": v(18927.44, -82997.93) * mm, "end": v(18784.54, -83590.54) * mm});
            skLineSegment(sketch, "E258", {"start": v(20508.48, -88630.93) * mm, "end": v(17730.6, -87961.06) * mm});
            skLineSegment(sketch, "E259", {"start": v(17730.6, -87961.06) * mm, "end": v(17953.9, -87035.1) * mm});
            skLineSegment(sketch, "E260", {"start": v(17868.52, -87876.74) * mm, "end": v(21127.89, -88662.72) * mm});
            skLineSegment(sketch, "E261", {"start": v(18475.87, -85358.13) * mm, "end": v(19068.48, -85501.04) * mm});
            skLineSegment(sketch, "E262", {"start": v(19068.48, -85501.04) * mm, "end": v(18604.03, -87427.03) * mm});
            skLineSegment(sketch, "E263", {"start": v(22990.05, -89229.35) * mm, "end": v(24017.18, -84969.95) * mm});
            skLineSegment(sketch, "E264", {"start": v(22878.93, -89202.56) * mm, "end": v(23906.07, -84943.15) * mm});
            skLineSegment(sketch, "E265", {"start": v(21390.84, -88059.87) * mm, "end": v(23057.56, -88461.79) * mm});
            skLineSegment(sketch, "E266", {"start": v(21417.63, -87948.75) * mm, "end": v(23084.36, -88350.67) * mm});
            skLineSegment(sketch, "E267", {"start": v(21355.11, -88208.02) * mm, "end": v(21651.42, -88279.47) * mm});
            skLineSegment(sketch, "E268", {"start": v(21651.42, -88279.47) * mm, "end": v(21532.33, -88773.32) * mm});
            skLineSegment(sketch, "E269", {"start": v(21532.33, -88773.32) * mm, "end": v(21236.02, -88701.86) * mm});
            skLineSegment(sketch, "E270", {"start": v(21627.6, -88378.24) * mm, "end": v(22096.75, -88491.38) * mm});
            skLineSegment(sketch, "E271", {"start": v(22096.75, -88491.38) * mm, "end": v(22025.3, -88787.68) * mm});
            skLineSegment(sketch, "E272", {"start": v(22025.3, -88787.68) * mm, "end": v(21556.15, -88674.55) * mm});
            skLineSegment(sketch, "E273", {"start": v(22810.64, -88402.25) * mm, "end": v(22632, -89143.01) * mm});
            skLineSegment(sketch, "E274", {"start": v(22763.36, -88273.27) * mm, "end": v(22736.56, -88384.38) * mm});
            skLineSegment(sketch, "E275", {"start": v(22170.75, -88130.36) * mm, "end": v(22143.95, -88241.48) * mm});
            skLineSegment(sketch, "E276", {"start": v(22157.35, -88185.92) * mm, "end": v(22749.96, -88328.82) * mm});
            skArc(sketch, "E277", {"start": v(22157.35, -88185.92) * mm, "mid": v(22250.8, -88678.76) * mm, "end": v(22682.25, -88934.65) * mm, "construction": true});
            skLineSegment(sketch, "E278", {"start": v(21846.35, -86170.91) * mm, "end": v(23513.08, -86572.84) * mm});
            skLineSegment(sketch, "E279", {"start": v(22010.25, -88091.66) * mm, "end": v(22438.96, -86313.82) * mm});
            skLineSegment(sketch, "E280", {"start": v(21873.15, -86059.8) * mm, "end": v(23539.87, -86461.72) * mm});
            skLineSegment(sketch, "E281", {"start": v(22087.5, -85170.88) * mm, "end": v(23754.23, -85572.8) * mm});
            skLineSegment(sketch, "E282", {"start": v(22762.07, -86274.16) * mm, "end": v(22976.42, -85385.24) * mm});
            skLineSegment(sketch, "E283", {"start": v(22114.3, -85059.76) * mm, "end": v(23781.02, -85461.69) * mm});
            skLineSegment(sketch, "E284", {"start": v(21873.15, -86059.8) * mm, "end": v(22976.42, -85385.24) * mm});
            skLineSegment(sketch, "E285", {"start": v(22087.5, -85170.88) * mm, "end": v(22762.07, -86274.16) * mm});
            skSolve(sketch);
        }
        {
            var Q0;
            Q0=makeQuery(id+"F8.imprint","IMPRINT",FACE,{"disambiguationData":[TD([[makeQuery(id+"F8.imprint","IMPRINT",EDGE,{"derivedFrom":sQuery(id+"F8.wireOp",EDGE,"E27")}),1.0]])]});
            var Q1;
            {var subQ11=sQuery(id+"F8.wireOp",EDGE,"E49");Q1=makeQuery(id+"F8.imprint","IMPRINT",FACE,{"disambiguationData":[TD([[makeQuery(id+"F8.imprint","IMPRINT",EDGE,{"derivedFrom":subQ11}),-1.0]])]});}
            var Q2;
            {var subQ0=sQuery(id+"F8.wireOp",EDGE,"E63");Q2=makeQuery(id+"F8.imprint","IMPRINT",FACE,{"disambiguationData":[TD([[makeQuery(id+"F8.imprint","IMPRINT",EDGE,{"derivedFrom":subQ0}),-1.0]])]});}
            var Q3;
            {var subQ4=sQuery(id+"F8.wireOp",EDGE,"rclvcfd8-MIHF-olu5-eLjo-lo3ld7nkITQP");var subQ5=sQuery(id+"F8.wireOp",EDGE,"E59");var subQ6=makeQuery(id+"F8.imprint","INTERSECT",VERTEX,{"derivedFrom":[subQ5,subQ4]});Q3=makeQuery(id+"F8.imprint","IMPRINT",FACE,{"disambiguationData":[TD([[makeQuery(id+"F8.imprint","IMPRINT",EDGE,{"disambiguationData":[TD([[subQ6,-1.0]])],"derivedFrom":subQ5}),-1.0]])]});}
            var Q4;
            {var subQ0=sQuery(id+"F8.wireOp",EDGE,"91OHXUqX-C3oE-HEue-zxtG-qKXiDudTgW1D");Q4=makeQuery(id+"F8.imprint","IMPRINT",FACE,{"disambiguationData":[TD([[makeQuery(id+"F8.imprint","IMPRINT",EDGE,{"derivedFrom":subQ0}),-1.0]])]});}
            var Q5;
            {var subQ0=sQuery(id+"F8.wireOp",EDGE,"E125");Q5=makeQuery(id+"F8.imprint","IMPRINT",FACE,{"disambiguationData":[TD([[makeQuery(id+"F8.imprint","IMPRINT",EDGE,{"derivedFrom":subQ0}),1.0]])]});}
            var Q6;
            {var subQ1=sQuery(id+"F8.wireOp",EDGE,"E100");Q6=makeQuery(id+"F8.imprint","IMPRINT",FACE,{"disambiguationData":[TD([[makeQuery(id+"F8.imprint","IMPRINT",EDGE,{"derivedFrom":subQ1}),-1.0]])]});}
            var Q7;
            {var subQ0=sQuery(id+"F8.wireOp",EDGE,"E122");Q7=makeQuery(id+"F8.imprint","IMPRINT",FACE,{"disambiguationData":[TD([[makeQuery(id+"F8.imprint","IMPRINT",EDGE,{"derivedFrom":subQ0}),-1.0]])]});}
            var Q8;
            {var subQ9=sQuery(id+"F8.wireOp",EDGE,"y9TLkgls-R7Ua-mZ38-rQrq-zVLpXJYmZp5l");Q8=makeQuery(id+"F8.imprint","IMPRINT",FACE,{"disambiguationData":[TD([[makeQuery(id+"F8.imprint","IMPRINT",EDGE,{"derivedFrom":subQ9}),1.0]])]});}
            var Q9;
            {var subQ5=sQuery(id+"F8.wireOp",EDGE,"GEOfW8i7-v1bV-P7JK-g7ps-RluW9onRIqib");Q9=makeQuery(id+"F8.imprint","IMPRINT",FACE,{"disambiguationData":[TD([[makeQuery(id+"F8.imprint","IMPRINT",EDGE,{"derivedFrom":subQ5}),1.0]])]});}
            var Q10;
            {var subQ0=sQuery(id+"F8.wireOp",EDGE,"7G9Qx8bP-DBMP-lqC7-5b62-GySUcdNvJU6V");var subQ1=sQuery(id+"F8.wireOp",EDGE,"vXCj9M6k-yY96-d7Ti-VudD-nu8TxWQPsee9");var subQ2=makeQuery(id+"F8.imprint","INTERSECT",VERTEX,{"derivedFrom":[subQ1,subQ0]});Q10=makeQuery(id+"F8.imprint","IMPRINT",FACE,{"disambiguationData":[TD([[makeQuery(id+"F8.imprint","IMPRINT",EDGE,{"disambiguationData":[TD([[subQ2,1.0]])],"derivedFrom":subQ1}),1.0]])]});}
            var Q11;
            {var subQ0=sQuery(id+"F8.wireOp",EDGE,"7G9Qx8bP-DBMP-lqC7-5b62-GySUcdNvJU6V");var subQ5=sQuery(id+"F8.wireOp",EDGE,"DJspllXv-pb2S-FSFw-zfOf-plQMQFauy2Zp");var subQ10=makeQuery(id+"F8.imprint","INTERSECT",VERTEX,{"derivedFrom":[subQ5,subQ0]});Q11=makeQuery(id+"F8.imprint","IMPRINT",FACE,{"disambiguationData":[TD([[makeQuery(id+"F8.imprint","IMPRINT",EDGE,{"disambiguationData":[TD([[subQ10,-1.0]])],"derivedFrom":subQ5}),1.0]])]});}
            var Q12;
            {var subQ0=sQuery(id+"F8.wireOp",EDGE,"dUWCwIAw-JhBd-akVE-Hmhs-d7drkbT7cW03");var subQ1=sQuery(id+"F8.wireOp",EDGE,"x7b1TImQ-eSQB-i5Y2-Ygrg-QIZ09I33ShdG");var subQ2=makeQuery(id+"F8.imprint","INTERSECT",VERTEX,{"derivedFrom":[subQ1,subQ0]});Q12=makeQuery(id+"F8.imprint","IMPRINT",FACE,{"disambiguationData":[TD([[makeQuery(id+"F8.imprint","IMPRINT",EDGE,{"disambiguationData":[TD([[subQ2,-1.0]])],"derivedFrom":subQ1}),-1.0]])]});}
            var Q13;
            {var subQ0=sQuery(id+"F8.wireOp",EDGE,"rNOulmPv-4JKR-VCrs-KXxh-W6KptRLK2svy");var subQ1=sQuery(id+"F8.wireOp",EDGE,"x7b1TImQ-eSQB-i5Y2-Ygrg-QIZ09I33ShdG");var subQ2=makeQuery(id+"F8.imprint","INTERSECT",VERTEX,{"derivedFrom":[subQ1,subQ0]});Q13=makeQuery(id+"F8.imprint","IMPRINT",FACE,{"disambiguationData":[TD([[makeQuery(id+"F8.imprint","IMPRINT",EDGE,{"disambiguationData":[TD([[subQ2,1.0]])],"derivedFrom":subQ1}),-1.0]])]});}
            var Q14;
            {var subQ1=sQuery(id+"F8.wireOp",EDGE,"eEUDFalC-DmD9-SJIB-ZcAk-zIuEDtrnNExR");var subQ6=sQuery(id+"F8.wireOp",EDGE,"dUWCwIAw-JhBd-akVE-Hmhs-d7drkbT7cW03");var subQ7=makeQuery(id+"F8.imprint","INTERSECT",VERTEX,{"derivedFrom":[subQ1,subQ6]});Q14=makeQuery(id+"F8.imprint","IMPRINT",FACE,{"disambiguationData":[TD([[makeQuery(id+"F8.imprint","IMPRINT",EDGE,{"disambiguationData":[TD([[subQ7,1.0]])],"derivedFrom":subQ1}),-1.0]])]});}
            var Q15;
            {var subQ4=sQuery(id+"F8.wireOp",EDGE,"AhaKkWxx-jGdp-S9RE-RZSQ-OpwDCgqlpkaN");var subQ5=sQuery(id+"F8.wireOp",EDGE,"eEUDFalC-DmD9-SJIB-ZcAk-zIuEDtrnNExR");var subQ6=makeQuery(id+"F8.imprint","INTERSECT",VERTEX,{"derivedFrom":[subQ5,subQ4]});Q15=makeQuery(id+"F8.imprint","IMPRINT",FACE,{"disambiguationData":[TD([[makeQuery(id+"F8.imprint","IMPRINT",EDGE,{"disambiguationData":[TD([[subQ6,-1.0]])],"derivedFrom":subQ4}),-1.0]])]});}
            var Q16;
            {var subQ16=sQuery(id+"F8.wireOp",EDGE,"E56.0");Q16=makeQuery(id+"F8.imprint","IMPRINT",FACE,{"disambiguationData":[TD([[makeQuery(id+"F8.imprint","IMPRINT",EDGE,{"derivedFrom":subQ16}),1.0]])]});}
            extrude(context, id + "F9", {"entities" : qUnion([Q0, Q1, Q2, Q3, Q4, Q5, Q6, Q7, Q8, Q9, Q10, Q11, Q12, Q13, Q14, Q15, Q16]), "operationType" : NewBodyOperationType.ADD, "depth" : 3048 * mm, "offsetDistance" : 25.4 * mm});
        }
    });
